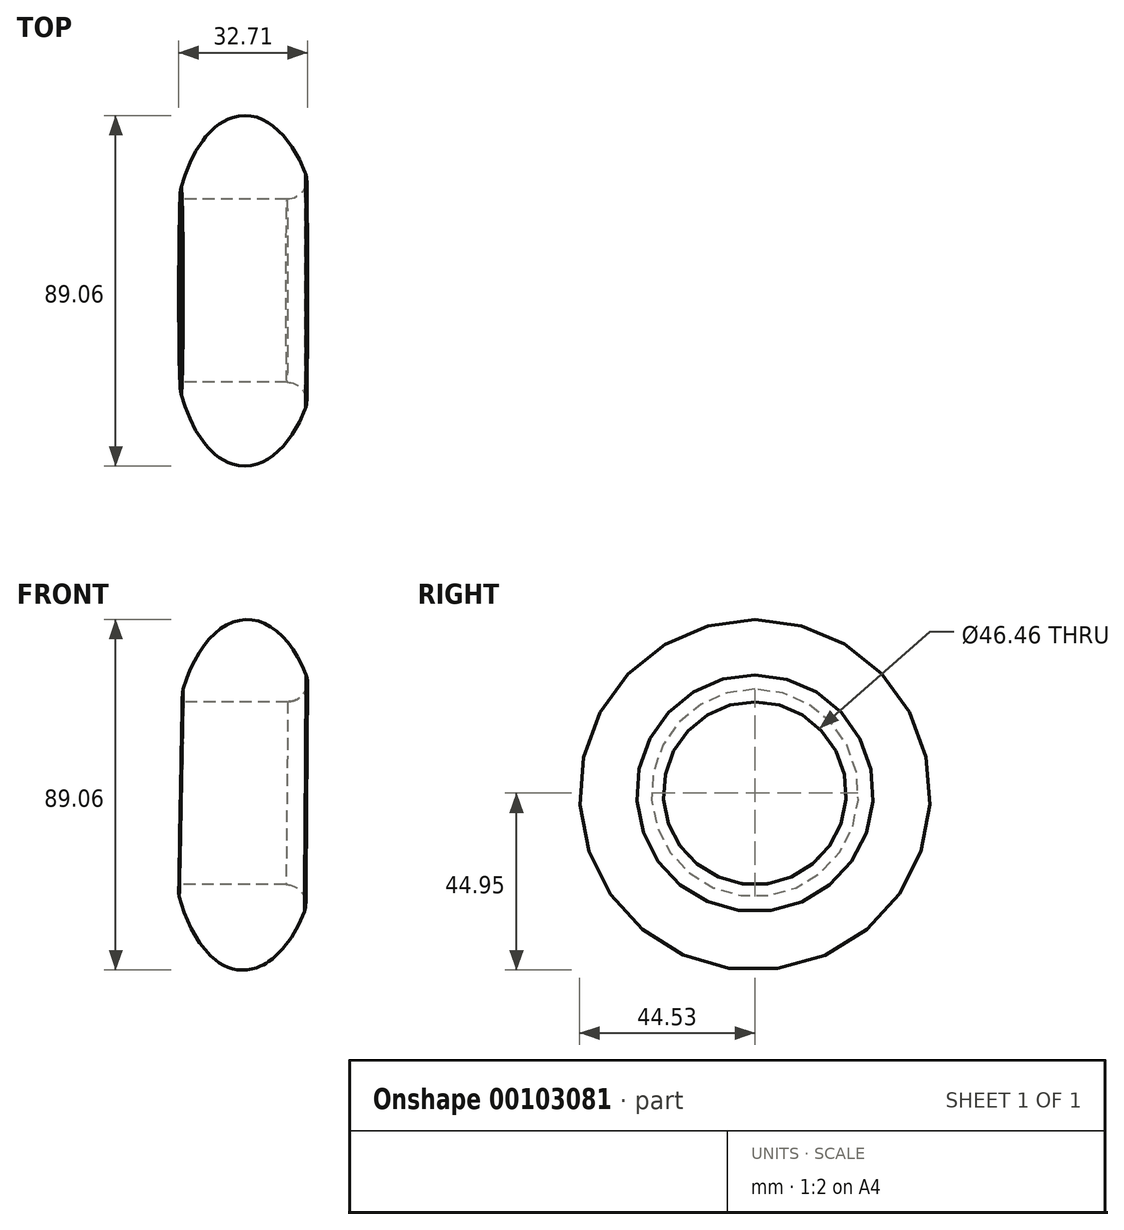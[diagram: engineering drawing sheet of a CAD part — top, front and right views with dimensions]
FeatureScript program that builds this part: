
annotation { "Feature Type Name" : "Feature", "Feature Type Description" : "" }
export const myFeature = defineFeature(function(context is Context, id is Id, definition is map)
    precondition{}
    {
        {
            var Q0;
            Q0=qCreatedBy(makeId("Front.planeOp"),FACE);
            var sketch = newSketch(context, id + "F0", { "sketchPlane" : qUnion([Q0])});
            skEllipticalArc(sketch, "E0", {});
            skLineSegment(sketch, "E1", {"start": v(-17.6, -0.15) * mm, "end": v(17.5, -0.7) * mm});
            const initialGuessF0  = {"E0": [0, 0.010217564180493355, 0, 1, 0.03389240615069866, 0.01849255147393423, 4.384295270515896, 1.8815988325944966]};
            skSetInitialGuess(sketch, initialGuessF0);
            skSolve(sketch);
        }
        {
            var Q0;
            Q0=makeQuery(id+"F0.imprint","IMPRINT",FACE,{"disambiguationData":[TD([[makeQuery(id+"F0.imprint","IMPRINT",EDGE,{"derivedFrom":sQuery(id+"F0.wireOp",EDGE,"E0")}),1.0]])]});
            var Q1;
            Q1=sQuery(id+"F0.wireOp",EDGE,"E1");
            var Q2;
            Q2=sQuery(id+"F0.wireOp",EDGE,"E1");
            revolve(context, id + "F1", {"entities" : qUnion([Q0]), "surfaceEntities" : qUnion([Q1]), "axis" : qUnion([Q2]), "revolveType" : RevolveType.FULL});
        }
        {
            var Q0;
            Q0=qCreatedBy(makeId("Right.planeOp"),FACE);
            var sketch = newSketch(context, id + "F2", { "sketchPlane" : qUnion([Q0])});
            skCircle(sketch, "E2", {"center": v(0, 0) * mm, "radius": 23.23 * mm});
            skSolve(sketch);
        }
        {
            var Q0;
            Q0 = qSketchRegion(id + "F2", true);
            extrude(context, id + "F3", {"entities" : qUnion([Q0]), "operationType" : NewBodyOperationType.REMOVE, "endBound" : BoundingType.THROUGH_ALL, "depth" : 20 * mm});
        }
        {
            var Q0;
            Q0=qCreatedBy(makeId("Right.planeOp"),FACE);
            var sketch = newSketch(context, id + "F4", { "sketchPlane" : qUnion([Q0])});
            skCircle(sketch, "E3", {"center": v(0, 0) * mm, "radius": 20 * mm});
            skSolve(sketch);
        }
        {
            var Q0;
            Q0 = qSketchRegion(id + "F4", true);
            extrude(context, id + "F5", {"entities" : qUnion([Q0]), "operationType" : NewBodyOperationType.REMOVE, "endBound" : BoundingType.THROUGH_ALL, "oppositeDirection" : true, "depth" : 25 * mm});
        }
        {
            var Q0;
            Q0=makeQuery(id+"F3.boolean.opBoolean","INTERSECT",EDGE,{"derivedFrom":[makeQuery(id+"F1.opRevolve","SWEPT_FACE",FACE,{"disambiguationData":[OSD([sQuery(id+"F0.wireOp",EDGE,"E0")])]}),makeQuery(id+"F3.opExtrude","SWEPT_FACE",FACE,{"disambiguationData":[OSD([sQuery(id+"F2.wireOp",EDGE,"E2")])]})]});
            var Q1;
            Q1=makeQuery(id+"F5.boolean.opBoolean","INTERSECT",EDGE,{"derivedFrom":[makeQuery(id+"F1.opRevolve","SWEPT_FACE",FACE,{"disambiguationData":[OSD([sQuery(id+"F0.wireOp",EDGE,"E0")])]}),makeQuery(id+"F5.opExtrude","SWEPT_FACE",FACE,{"disambiguationData":[OSD([sQuery(id+"F4.wireOp",EDGE,"E3")])]})]});
            fillet(context, id + "F6", {"entities" : qUnion([Q0, Q1]), "radius" : 5 * mm, "tangentPropagation" : true, "allowEdgeOverflow" : false});
        }
        {
            var Q0;
            Q0=makeQuery(id+"F3.boolean.opBoolean","COPY",FACE,{"derivedFrom":makeQuery(id+"F3.opExtrude","CAP_FACE",FACE,{"disambiguationData":[OSD([sQuery(id+"F2.wireOp",EDGE,"E2")])],"isStart":true})});
            extrude(context, id + "F7", {"entities" : qUnion([Q0]), "operationType" : NewBodyOperationType.REMOVE, "endBound" : BoundingType.THROUGH_ALL, "oppositeDirection" : true, "depth" : 25 * mm});
        }
    });
